# Revit family: Accessory-Flush_Actuator_Plate-KOHLER-Lynk-K-75890T_1
name_source: partatom
category: Specialty Equipment
revit_build: Autodesk Revit 2017 (Build: 20160225_1515(x64)
units: mm (PartAtom-declared; Revit-internal decimal feet)

## family parameters
Cut with Voids When Loaded = No
Host = Face
OmniClass Number = 23.31.25.00
OmniClass Title = Toilet and Bath Specialties
Part Type = Normal
Room Calculation Point = No
Round Connector Dimension = Use Diameter
Shared = No

## types (2) — shared parameters
ADA Compliant = No
Assembly Code = C1030200
Date Modified = 01/08/2021
Default Elevation = 42"
Finish = KOHLER-Plastic-CP-Polished_Chrome
Height = 6 5/16"
Length = 3/8"
Manufacturer = KOHLER Co.
Master Format 2014 = 10 28 00
Master Format 2014 Name = Toilet, Bath, and Laundry Accessories
Material = Plastic
Product Name = Lynk
URL = http://www.kohler.com.cn
WaterSense Certified = No
Width = 8 7/8"

## per-type parameters (varying)
| type | Description | Model | Product Documentation Link | Product Page URL | Type |
| CP- Polished Chrome | Concealed Water Tank Panel | K-75890T-CP | https://files.kohler.com.cn | https://www.kohler.com.cn | 1 |
| PNE-CP- Polished Chrome | Pneumatic Hidden Water Tank Panel | K-75890T-PNE-CP |  |  | 2 |

## geometry (parser evidence)
native form markers: Sweep x5
no freeform markers — native parametric forms only
